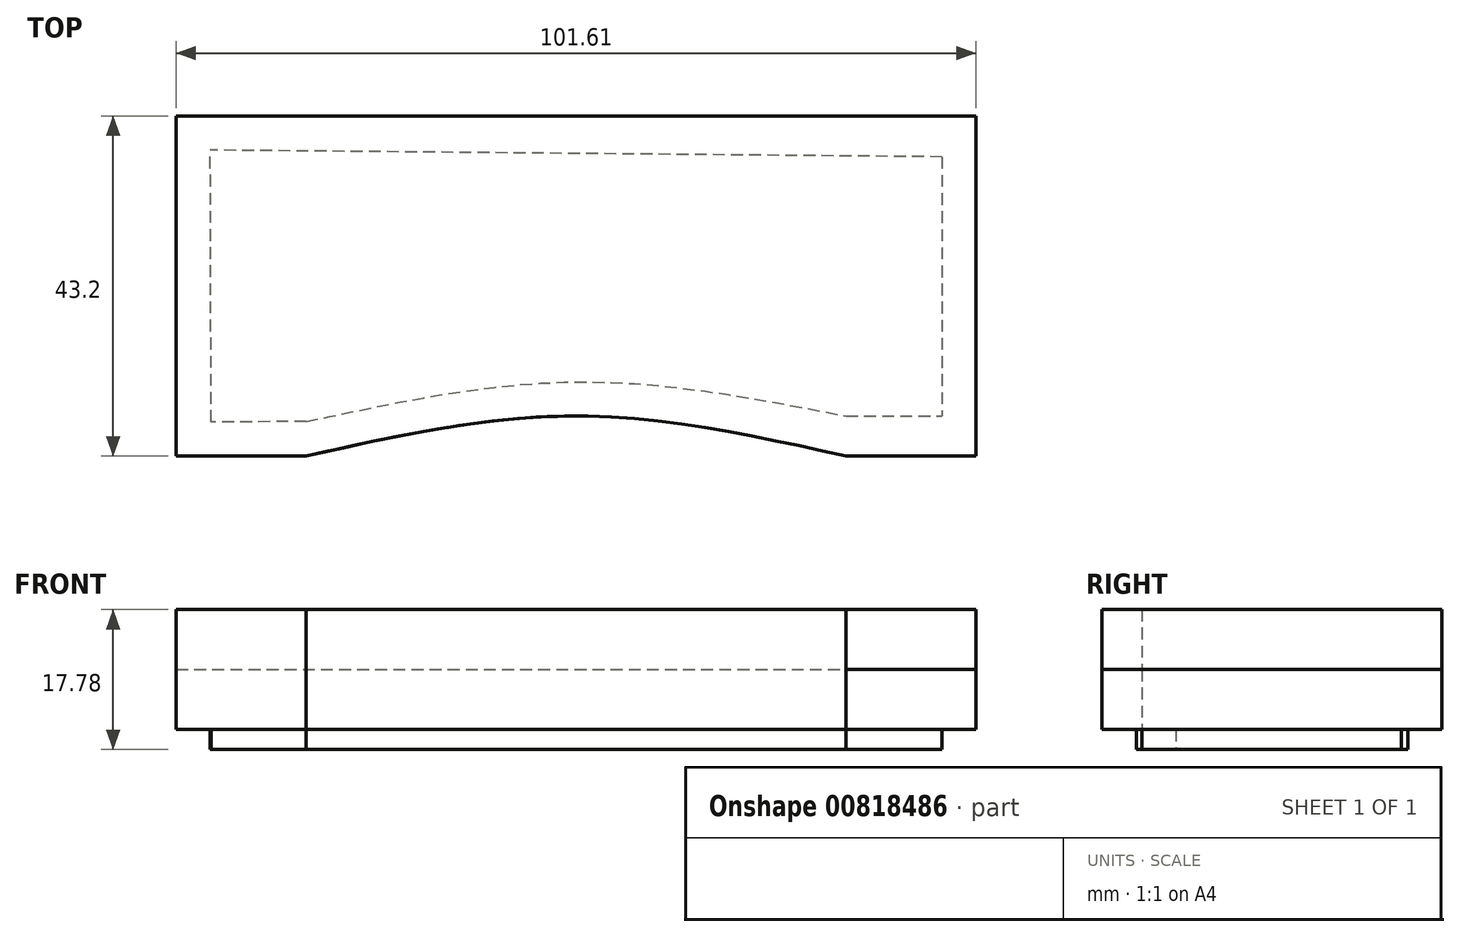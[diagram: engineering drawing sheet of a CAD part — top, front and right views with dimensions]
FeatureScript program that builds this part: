
annotation { "Feature Type Name" : "Feature", "Feature Type Description" : "" }
export const myFeature = defineFeature(function(context is Context, id is Id, definition is map)
    precondition{}
    {
        {
            var Q0;
            Q0=qCreatedBy(makeId("Top.planeOp"),FACE);
            var sketch = newSketch(context, id + "F0", { "sketchPlane" : qUnion([Q0])});
            skLineSegment(sketch, "E0", {"start": v(-46.46, 17.27) * mm, "end": v(-46.35, -17.26) * mm});
            skLineSegment(sketch, "E1", {"start": v(-46.35, -17.26) * mm, "end": v(-34.27, -17.22) * mm});
            skLineSegment(sketch, "E2", {"start": v(-46.46, 17.27) * mm, "end": v(46.49, 16.4) * mm});
            skLineSegment(sketch, "E3", {"start": v(46.49, -16.51) * mm, "end": v(46.49, 16.4) * mm});
            skLineSegment(sketch, "E4", {"start": v(46.49, -16.51) * mm, "end": v(34.3, -16.51) * mm});
            skFitSpline(sketch, "E5", {"points": [v(-34.27, -17.22) * mm, v(0, -12.18) * mm, v(34.3, -16.51) * mm], "startDerivative": vector(68.47, 14.76) * mm, "endDerivative": vector(68.66, -13.35) * mm});
            skSolve(sketch);
        }
        {
            var Q0;
            Q0=qCreatedBy(makeId("Top.planeOp"),FACE);
            var sketch = newSketch(context, id + "F1", { "sketchPlane" : qUnion([Q0])});
            skLineSegment(sketch, "E6", {"start": v(0, 21.58) * mm, "end": v(50.8, 21.58) * mm});
            skLineSegment(sketch, "E7", {"start": v(0, 21.58) * mm, "end": v(-50.8, 21.58) * mm});
            skLineSegment(sketch, "E8", {"start": v(-50.8, 21.58) * mm, "end": v(-50.8, -21.59) * mm});
            skLineSegment(sketch, "E9", {"start": v(-50.8, -21.59) * mm, "end": v(-34.3, -21.59) * mm});
            skLineSegment(sketch, "E10", {"start": v(50.8, 21.58) * mm, "end": v(50.8, -21.6) * mm});
            skLineSegment(sketch, "E11", {"start": v(50.8, -21.6) * mm, "end": v(34.3, -21.6) * mm});
            skFitSpline(sketch, "E12", {"points": [v(-34.3, -21.59) * mm, v(0, -16.5) * mm, v(34.3, -21.6) * mm], "startDerivative": vector(68.6, 15.24) * mm, "endDerivative": vector(68.6, -15.27) * mm});
            skSolve(sketch);
        }
        {
            var Q0;
            Q0=qCreatedBy(makeId("Top.planeOp"),FACE);
            var sketch = newSketch(context, id + "F2", { "sketchPlane" : qUnion([Q0])});
            skLineSegment(sketch, "E13", {"start": v(0, 21.6) * mm, "end": v(50.81, 21.6) * mm});
            skLineSegment(sketch, "E14", {"start": v(0, 21.6) * mm, "end": v(-50.8, 21.6) * mm});
            skLineSegment(sketch, "E15", {"start": v(-50.8, 21.6) * mm, "end": v(-50.8, -21.6) * mm});
            skLineSegment(sketch, "E16", {"start": v(-50.8, -21.6) * mm, "end": v(-34.3, -21.6) * mm});
            skLineSegment(sketch, "E17", {"start": v(50.81, 21.6) * mm, "end": v(50.81, -21.59) * mm});
            skLineSegment(sketch, "E18", {"start": v(50.81, -21.59) * mm, "end": v(34.31, -21.59) * mm});
            skFitSpline(sketch, "E19", {"points": [v(-34.3, -21.6) * mm, v(0, -16.5) * mm, v(34.31, -21.59) * mm], "startDerivative": vector(68.59, 15.26) * mm, "endDerivative": vector(68.62, -15.24) * mm});
            skSolve(sketch);
        }
        {
            var Q0;
            Q0 = qSketchRegion(id + "F1", true);
            extrude(context, id + "F3", {"entities" : qUnion([Q0]), "depth" : 7.62 * mm, "offsetDistance" : 25.4 * mm});
        }
        {
            var Q0;
            Q0 = qSketchRegion(id + "F0", true);
            extrude(context, id + "F4", {"entities" : qUnion([Q0]), "operationType" : NewBodyOperationType.ADD, "oppositeDirection" : true, "depth" : 10.16 * mm, "offsetDistance" : 25.4 * mm});
        }
        {
            var Q0;
            Q0 = qSketchRegion(id + "F2", true);
            extrude(context, id + "F5", {"entities" : qUnion([Q0]), "operationType" : NewBodyOperationType.ADD, "oppositeDirection" : true, "depth" : 7.62 * mm, "offsetDistance" : 25.4 * mm});
        }
    });
